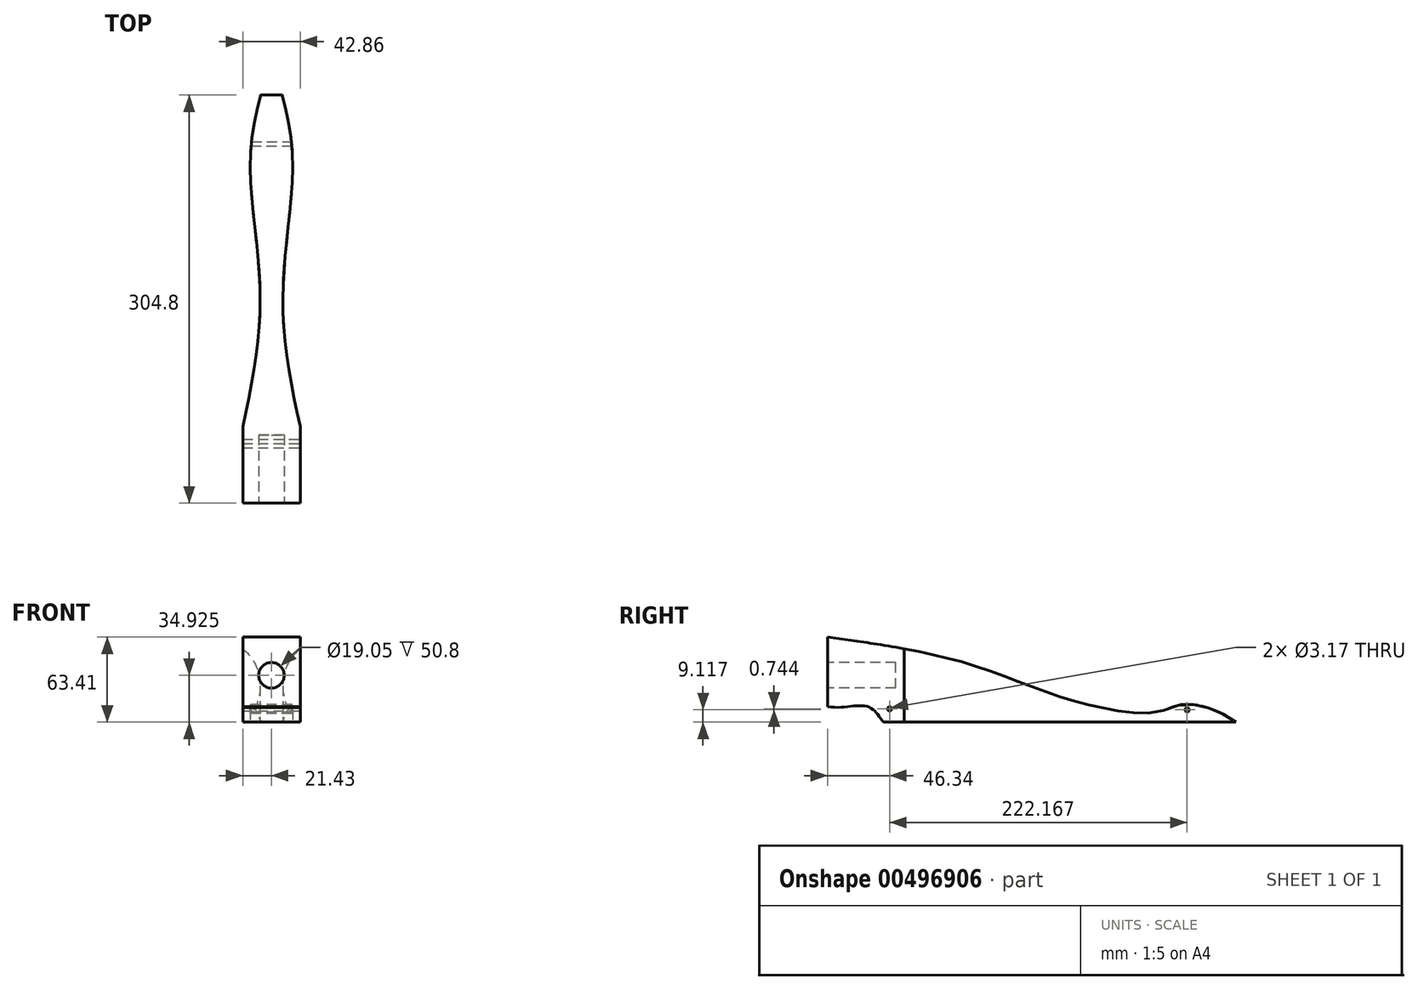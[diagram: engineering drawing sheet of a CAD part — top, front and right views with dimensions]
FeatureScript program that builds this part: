
annotation { "Feature Type Name" : "Feature", "Feature Type Description" : "" }
export const myFeature = defineFeature(function(context is Context, id is Id, definition is map)
    precondition{}
    {
        {
            var Q0;
            Q0=qCreatedBy(makeId("Right.planeOp"),FACE);
            var sketch = newSketch(context, id + "F0", { "sketchPlane" : qUnion([Q0])});
            skLineSegment(sketch, "E0", {"start": v(-152.4, 0) * mm, "end": v(152.4, 0) * mm});
            skLineSegment(sketch, "E1", {"start": v(-152.4, 0) * mm, "end": v(-152.4, 69.85) * mm});
            skLineSegment(sketch, "E2", {"start": v(152.4, 0) * mm, "end": v(152.4, 19.05) * mm});
            skLineSegment(sketch, "E3", {"start": v(152.4, 19.05) * mm, "end": v(-152.4, 69.85) * mm});
            skPoint(sketch, "E4.endSnap0", {"position": v(-152.4, 34.93) * mm});
            skLineSegment(sketch, "E5.0", {"start": v(-95.25, 50.8) * mm, "end": v(-152.4, 50.8) * mm, "construction": true});
            skLineSegment(sketch, "E5.1", {"start": v(-95.25, 50.8) * mm, "end": v(-95.25, 19.05) * mm, "construction": true});
            skLineSegment(sketch, "E5.2", {"start": v(-95.25, 19.05) * mm, "end": v(-152.4, 19.05) * mm, "construction": true});
            skSolve(sketch);
        }
        {
            var Q0;
            Q0=makeQuery(id+"F0.imprint","IMPRINT",FACE,{"disambiguationData":[TD([[makeQuery(id+"F0.imprint","IMPRINT",EDGE,{"derivedFrom":sQuery(id+"F0.wireOp",EDGE,"E0")}),1.0]])]});
            extrude(context, id + "F1", {"entities" : qUnion([Q0]), "depth" : 42.86 * mm, "symmetric" : true});
        }
        {
            var Q0;
            Q0=makeQuery(id+"F1.opExtrude","SWEPT_FACE",FACE,{"disambiguationData":[OSD([sQuery(id+"F0.wireOp",EDGE,"E1")])]});
            var sketch = newSketch(context, id + "F2", { "sketchPlane" : qUnion([Q0])});
            skLineSegment(sketch, "E6", {"start": v(21.43, 34.93) * mm, "end": v(0, 34.93) * mm, "construction": true});
            skCircle(sketch, "E7", {"center": v(0, 34.93) * mm, "radius": 9.53 * mm});
            skSolve(sketch);
        }
        {
            var Q0;
            Q0=makeQuery(id+"F2.imprint","IMPRINT",FACE,{"disambiguationData":[TD([[makeQuery(id+"F2.imprint","IMPRINT",EDGE,{"derivedFrom":sQuery(id+"F2.wireOp",EDGE,"E7")}),1.0]])]});
            var Q1;
            Q1=sQuery(id+"F2.wireOp",EDGE,"E7");
            extrude(context, id + "F3", {"entities" : qUnion([Q0]), "operationType" : NewBodyOperationType.REMOVE, "surfaceEntities" : qUnion([Q1]), "oppositeDirection" : true, "depth" : 50.8 * mm});
        }
        {
            var Q0;
            Q0=makeQuery(id+"F1.opExtrude","CAP_FACE",FACE,{"disambiguationData":[OSD([sQuery(id+"F0.wireOp",EDGE,"E0"),sQuery(id+"F0.wireOp",EDGE,"E1"),sQuery(id+"F0.wireOp",EDGE,"E2"),sQuery(id+"F0.wireOp",EDGE,"E3")])],"isStart":false});
            var sketch = newSketch(context, id + "F4", { "sketchPlane" : qUnion([Q0])});
            skLineSegment(sketch, "E8", {"start": v(-152.4, 34.93) * mm, "end": v(-152.4, 44.45) * mm, "construction": true});
            skLineSegment(sketch, "E9.0", {"start": v(-95.25, 19.05) * mm, "end": v(-152.4, 19.05) * mm, "construction": true});
            skLineSegment(sketch, "E9.1", {"start": v(-95.25, 50.8) * mm, "end": v(-95.25, 19.05) * mm, "construction": true});
            skLineSegment(sketch, "E9.2", {"start": v(-152.4, 50.8) * mm, "end": v(-95.25, 50.8) * mm, "construction": true});
            skLineSegment(sketch, "E10", {"start": v(57.15, 0) * mm, "end": v(57.15, 34.93) * mm, "construction": true});
            skLineSegment(sketch, "E11", {"start": v(-152.4, 44.45) * mm, "end": v(-101.6, 44.45) * mm, "construction": true});
            skLineSegment(sketch, "E12", {"start": v(-101.6, 44.45) * mm, "end": v(-101.6, 25.4) * mm, "construction": true});
            skLineSegment(sketch, "E13", {"start": v(-101.6, 25.4) * mm, "end": v(-152.4, 25.4) * mm, "construction": true});
            skPoint(sketch, "E14.5.internal.snap0", {"position": v(57.15, 17.46) * mm});
            skFitSpline(sketch, "E15", {"points": [v(-152.4, 63.41) * mm, v(-113.47, 57.83) * mm, v(-45.2, 42.87) * mm, v(27.07, 17.16) * mm, v(93.45, 7.23) * mm, v(112.27, 13.06) * mm, v(152.4, 0) * mm], "startDerivative": vector(245.15, -33.08) * mm, "endDerivative": vector(239.19, -187.02) * mm});
            skFitSpline(sketch, "E16", {"points": [v(-152.4, 11.53) * mm, v(-122.59, 11.59) * mm, v(-110.85, 0) * mm], "startDerivative": vector(58.44, -10.48) * mm, "endDerivative": vector(22.3, -32.6) * mm});
            skCircle(sketch, "E17", {"center": v(-106.06, 9.86) * mm, "radius": 1.59 * mm});
            skCircle(sketch, "E18", {"center": v(116.1, 9.12) * mm, "radius": 1.59 * mm});
            skSolve(sketch);
        }
        {
            var Q0;
            Q0=makeQuery(id+"F1.opExtrude","SWEPT_FACE",FACE,{"disambiguationData":[OSD([sQuery(id+"F0.wireOp",EDGE,"E0")])]});
            var sketch = newSketch(context, id + "F5", { "sketchPlane" : qUnion([Q0])});
            skLineSegment(sketch, "E19", {"start": v(0, 152.4) * mm, "end": v(0, -152.4) * mm, "construction": true});
            skLineSegment(sketch, "E20", {"start": v(21.43, -57.15) * mm, "end": v(-21.43, -57.15) * mm, "construction": true});
            skLineSegment(sketch, "E21", {"start": v(15.88, 152.4) * mm, "end": v(15.88, 95.25) * mm, "construction": true});
            skLineSegment(sketch, "E22", {"start": v(15.88, 95.25) * mm, "end": v(-15.87, 95.25) * mm, "construction": true});
            skLineSegment(sketch, "E23", {"start": v(-15.87, 95.25) * mm, "end": v(-15.87, 152.4) * mm, "construction": true});
            skLineSegment(sketch, "E24", {"start": v(0, 152.4) * mm, "end": v(-9.53, 152.4) * mm, "construction": true});
            skLineSegment(sketch, "E25", {"start": v(-9.53, 152.4) * mm, "end": v(-9.53, 101.6) * mm, "construction": true});
            skLineSegment(sketch, "E26", {"start": v(-9.52, 101.6) * mm, "end": v(9.53, 101.6) * mm, "construction": true});
            skLineSegment(sketch, "E27", {"start": v(9.53, 101.6) * mm, "end": v(9.53, 152.4) * mm, "construction": true});
            skFitSpline(sketch, "E28", {"points": [v(-21.43, 95.25) * mm, v(-8.47, 0) * mm, v(-15.87, -100.14) * mm, v(-8.07, -152.4) * mm], "startDerivative": vector(54.51, -255.33) * mm, "endDerivative": vector(43.44, -177.12) * mm});
            skFitSpline(sketch, "E29.MirrorCS", {"points": [v(21.43, 95.25) * mm, v(8.47, 0) * mm, v(15.87, -100.14) * mm, v(8.07, -152.4) * mm], "startDerivative": vector(-54.51, -255.33) * mm, "endDerivative": vector(-43.44, -177.12) * mm});
            skSolve(sketch);
        }
        {
            var Q0;
            Q0 = qSketchRegion(id + "F4", true);
            var Q1;
            {var subQ0=sQuery(id+"F4.wireOp",EDGE,"E15");Q1=makeQuery(id+"F4.imprint","IMPRINT",FACE,{"disambiguationData":[TD([[makeQuery(id+"F4.imprint","IMPRINT",EDGE,{"derivedFrom":subQ0}),1.0]])]});}
            extrude(context, id + "F6", {"entities" : qUnion([Q0, Q1]), "operationType" : NewBodyOperationType.REMOVE, "endBound" : BoundingType.THROUGH_ALL, "oppositeDirection" : true, "depth" : 25.4 * mm});
        }
        {
            var Q0;
            Q0 = qSketchRegion(id + "F5", true);
            var Q1;
            {var subQ0=sQuery(id+"F5.wireOp",EDGE,"E29.MirrorCS");Q1=makeQuery(id+"F5.imprint","IMPRINT",FACE,{"disambiguationData":[TD([[makeQuery(id+"F5.imprint","IMPRINT",EDGE,{"derivedFrom":subQ0}),1.0]])]});}
            var Q2;
            {var subQ0=sQuery(id+"F5.wireOp",EDGE,"E28");Q2=makeQuery(id+"F5.imprint","IMPRINT",FACE,{"disambiguationData":[TD([[makeQuery(id+"F5.imprint","IMPRINT",EDGE,{"derivedFrom":subQ0}),-1.0]])]});}
            extrude(context, id + "F7", {"entities" : qUnion([Q0, Q1, Q2]), "operationType" : NewBodyOperationType.REMOVE, "endBound" : BoundingType.THROUGH_ALL, "oppositeDirection" : true, "depth" : 25.4 * mm});
        }
        {
            var Q0;
            {var subQ0=sQuery(id+"F4.wireOp",EDGE,"E16");Q0=makeQuery(id+"F4.imprint","IMPRINT",FACE,{"disambiguationData":[TD([[makeQuery(id+"F4.imprint","IMPRINT",EDGE,{"derivedFrom":subQ0}),-1.0]])]});}
            extrude(context, id + "F8", {"entities" : qUnion([Q0]), "operationType" : NewBodyOperationType.REMOVE, "endBound" : BoundingType.THROUGH_ALL, "oppositeDirection" : true, "depth" : 25.4 * mm});
        }
        {
            var Q0;
            Q0 = qSketchRegion(id + "F4", true);
            extrude(context, id + "F9", {"entities" : qUnion([Q0]), "operationType" : NewBodyOperationType.REMOVE, "endBound" : BoundingType.THROUGH_ALL, "oppositeDirection" : true, "depth" : 25.4 * mm});
        }
    });
